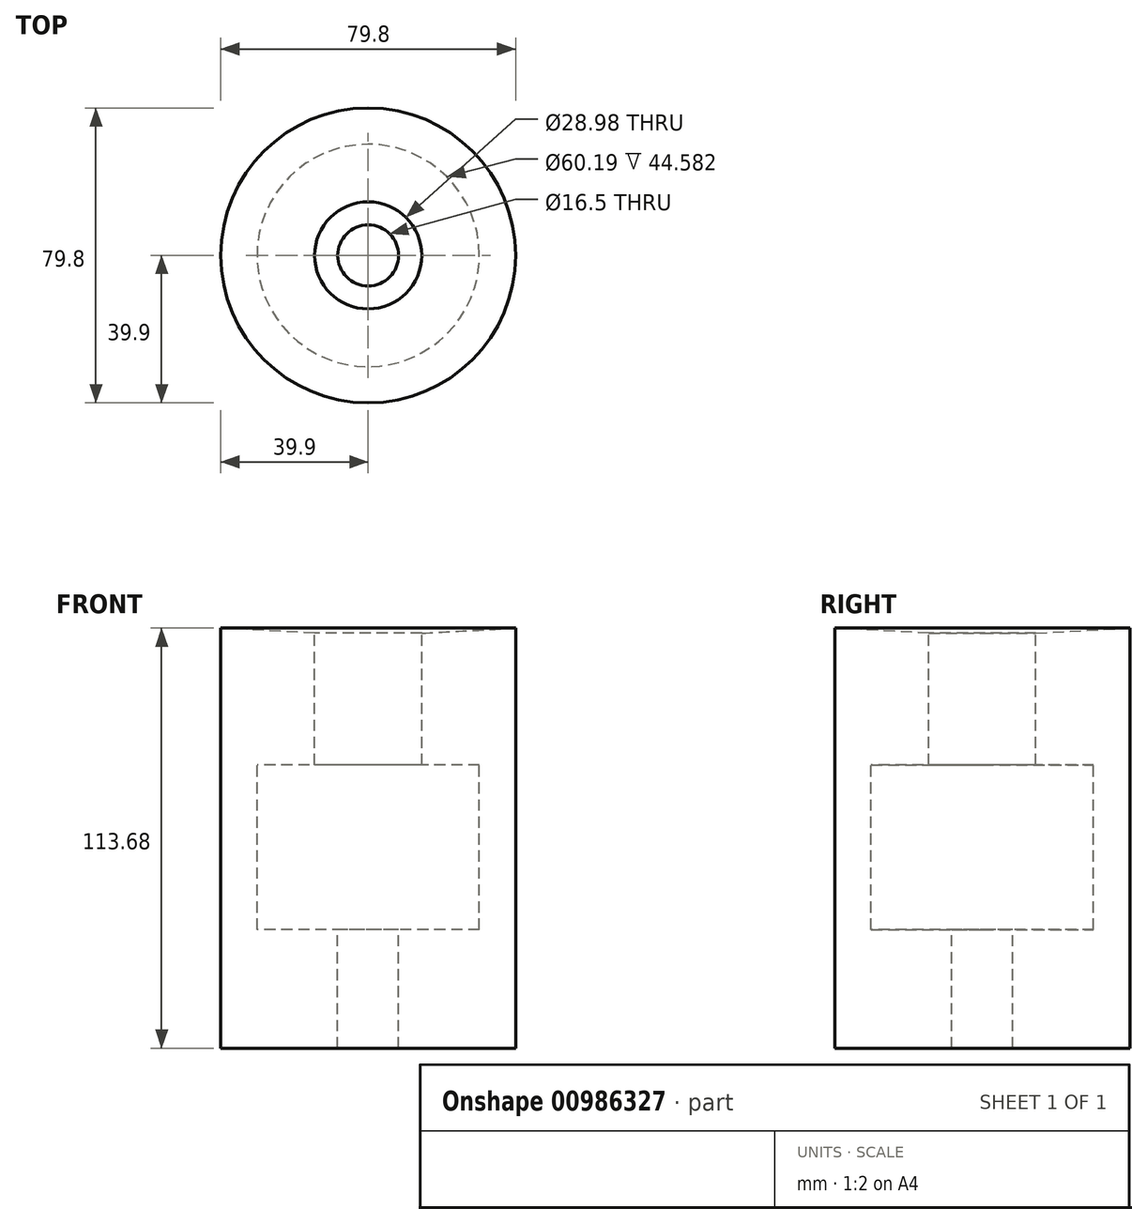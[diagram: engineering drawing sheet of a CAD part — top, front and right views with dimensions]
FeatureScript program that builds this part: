
annotation { "Feature Type Name" : "Feature", "Feature Type Description" : "" }
export const myFeature = defineFeature(function(context is Context, id is Id, definition is map)
    precondition{}
    {
        {
            var Q0;
            Q0=qCreatedBy(makeId("Front.planeOp"),FACE);
            var sketch = newSketch(context, id + "F0", { "sketchPlane" : qUnion([Q0])});
            skLineSegment(sketch, "E0", {"start": v(14.49, 49.26) * mm, "end": v(14.49, 13.6) * mm});
            skLineSegment(sketch, "E1", {"start": v(14.49, 13.6) * mm, "end": v(30.1, 13.6) * mm});
            skLineSegment(sketch, "E2", {"start": v(30.1, 13.6) * mm, "end": v(30.1, -30.98) * mm});
            skLineSegment(sketch, "E3", {"start": v(30.1, -30.98) * mm, "end": v(8.25, -30.98) * mm});
            skLineSegment(sketch, "E4", {"start": v(8.25, -30.98) * mm, "end": v(8.25, -63.08) * mm});
            skLineSegment(sketch, "E5", {"start": v(8.25, -63.08) * mm, "end": v(39.9, -63.08) * mm});
            skLineSegment(sketch, "E6", {"start": v(39.9, -63.08) * mm, "end": v(39.9, 50.6) * mm});
            skLineSegment(sketch, "E7", {"start": v(39.9, 50.6) * mm, "end": v(14.49, 49.26) * mm});
            skLineSegment(sketch, "E8", {"start": v(0, 66.86) * mm, "end": v(0, -73.1) * mm, "construction": true});
            skSolve(sketch);
        }
        {
            var Q0;
            Q0=makeQuery(id+"F0.imprint","IMPRINT",FACE,{"disambiguationData":[TD([[makeQuery(id+"F0.imprint","IMPRINT",EDGE,{"derivedFrom":sQuery(id+"F0.wireOp",EDGE,"E0")}),1.0]])]});
            var Q1;
            Q1=sQuery(id+"F0.wireOp",EDGE,"E8");
            revolve(context, id + "F1", {"surfaceOperationType" : NewSurfaceOperationType.ADD, "entities" : qUnion([Q0]), "axis" : qUnion([Q1]), "revolveType" : RevolveType.FULL});
        }
    });
